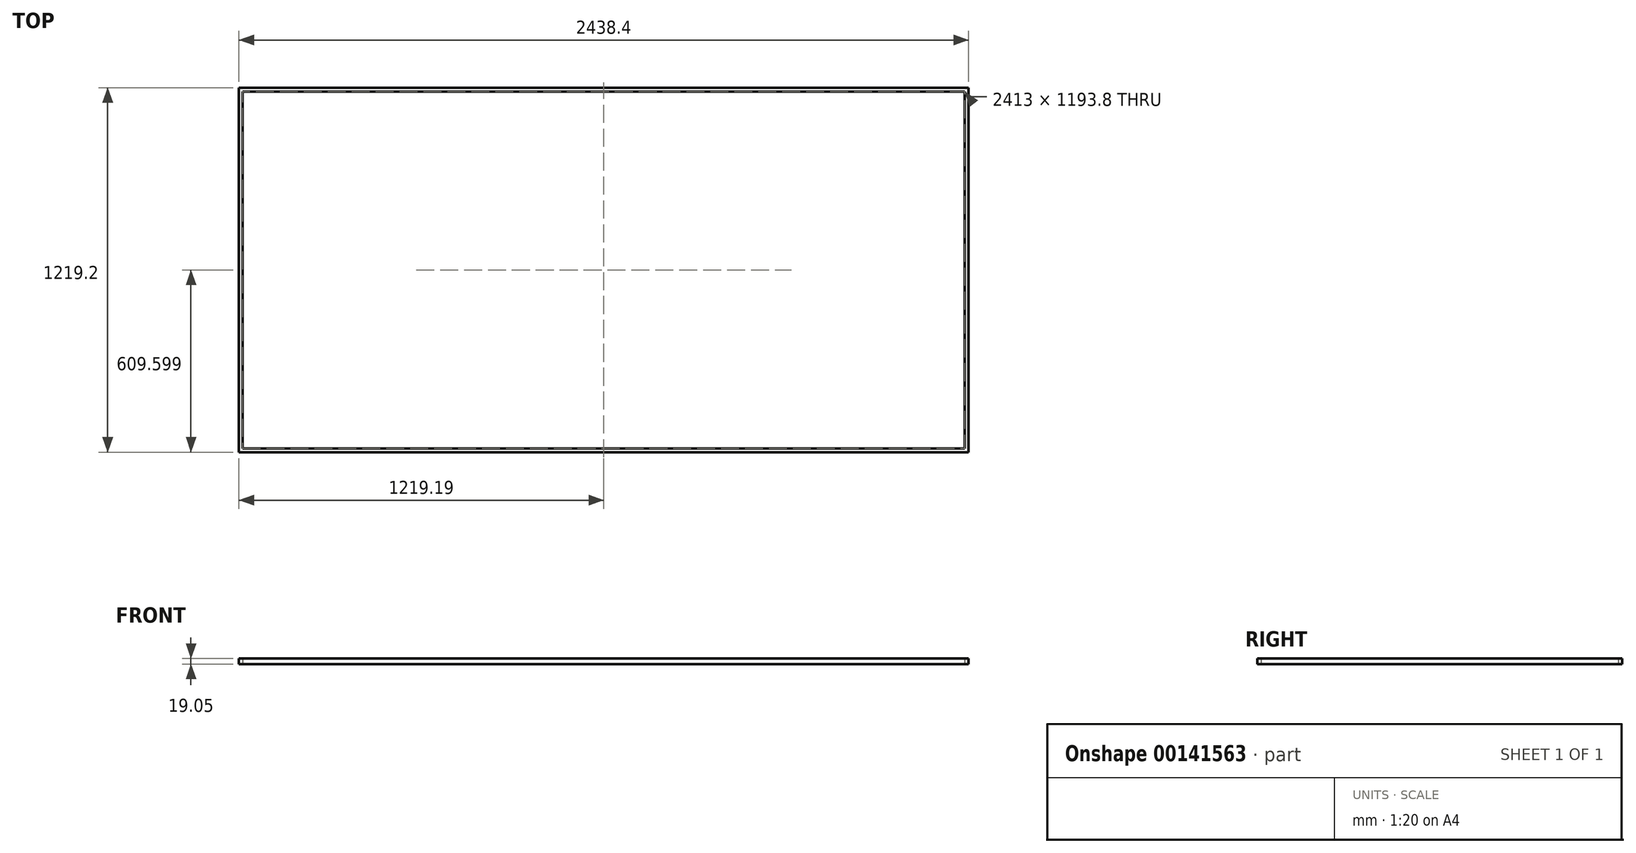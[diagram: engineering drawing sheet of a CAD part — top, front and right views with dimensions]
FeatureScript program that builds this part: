
annotation { "Feature Type Name" : "Feature", "Feature Type Description" : "" }
export const myFeature = defineFeature(function(context is Context, id is Id, definition is map)
    precondition{}
    {
        {
            var Q0;
            Q0=qCreatedBy(makeId("Top.planeOp"),FACE);
            var sketch = newSketch(context, id + "F0", { "sketchPlane" : qUnion([Q0])});
            skLineSegment(sketch, "E0.bottom", {"start": v(-132.11, -81.43) * mm, "end": v(2306.29, -81.43) * mm});
            skLineSegment(sketch, "E0.top", {"start": v(-132.11, 1137.77) * mm, "end": v(2306.29, 1137.77) * mm});
            skLineSegment(sketch, "E0.left", {"start": v(-132.11, -81.43) * mm, "end": v(-132.11, 1137.77) * mm});
            skLineSegment(sketch, "E0.right", {"start": v(2306.29, -81.43) * mm, "end": v(2306.29, 1137.77) * mm});
            skLineSegment(sketch, "E1.0", {"start": v(-119.41, -68.73) * mm, "end": v(-119.41, 1125.07) * mm});
            skLineSegment(sketch, "E1.1", {"start": v(-119.41, -68.73) * mm, "end": v(2293.59, -68.73) * mm});
            skLineSegment(sketch, "E1.2", {"start": v(2293.59, -68.73) * mm, "end": v(2293.59, 1125.07) * mm});
            skLineSegment(sketch, "E1.3", {"start": v(-119.41, 1125.07) * mm, "end": v(2293.59, 1125.07) * mm});
            skSolve(sketch);
        }
        {
            var Q0;
            Q0=makeQuery(id+"F0.imprint","IMPRINT",FACE,{"disambiguationData":[TD([[makeQuery(id+"F0.imprint","IMPRINT",EDGE,{"derivedFrom":sQuery(id+"F0.wireOp",EDGE,"E0.bottom")}),1.0]])]});
            extrude(context, id + "F1", {"entities" : qUnion([Q0]), "depth" : 19.05 * mm});
        }
    });
